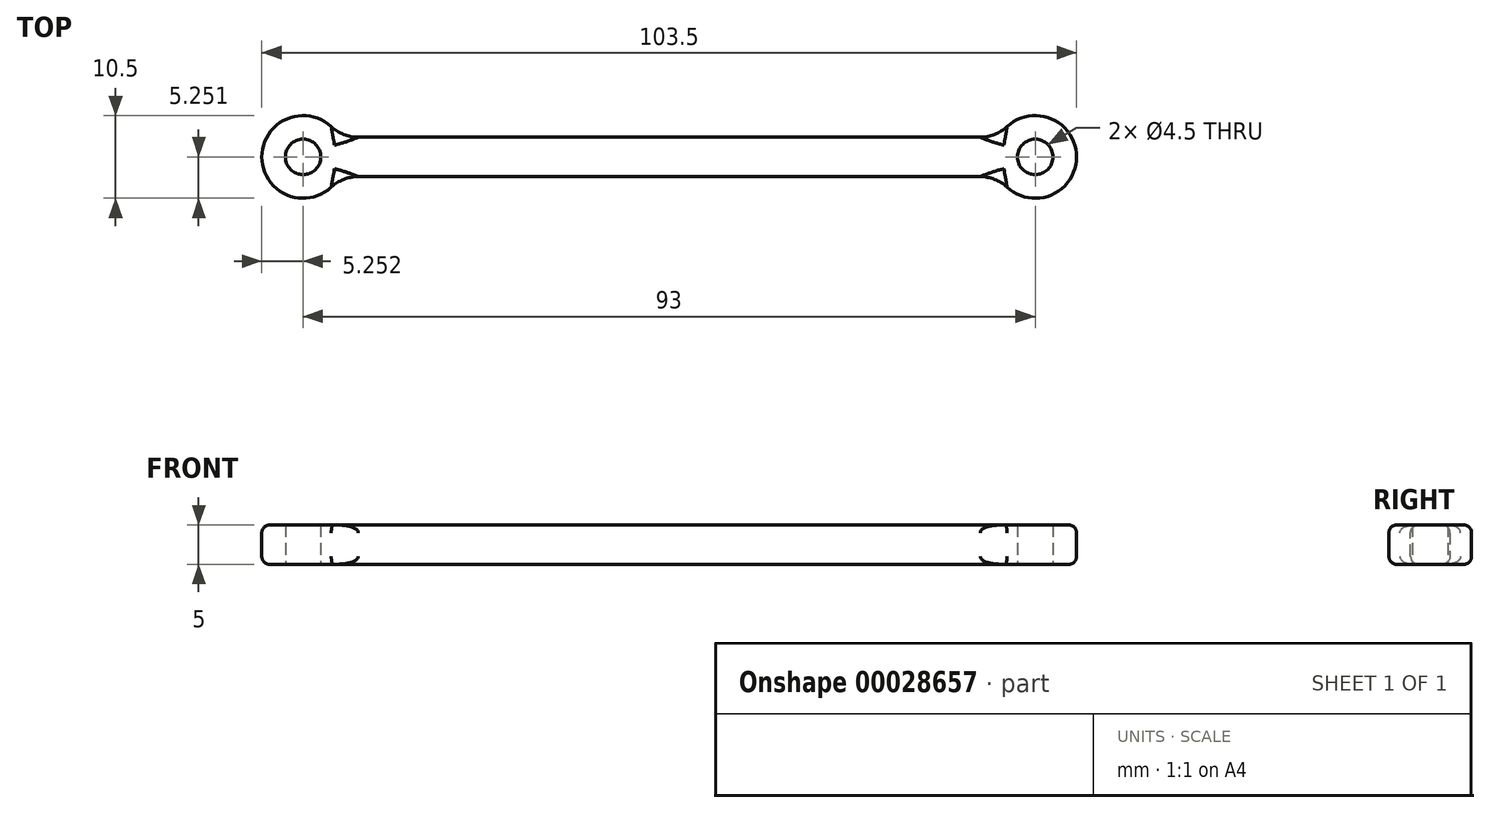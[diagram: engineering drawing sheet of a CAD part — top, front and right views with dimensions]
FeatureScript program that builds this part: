
annotation { "Feature Type Name" : "Feature", "Feature Type Description" : "" }
export const myFeature = defineFeature(function(context is Context, id is Id, definition is map)
    precondition{}
    {
        {
            var Q0;
            Q0=qCreatedBy(makeId("Top.planeOp"),FACE);
            var sketch = newSketch(context, id + "F0", { "sketchPlane" : qUnion([Q0])});
            skLineSegment(sketch, "E0.bottom", {"start": v(-37.64, 2.63) * mm, "end": v(55.36, 2.63) * mm});
            skLineSegment(sketch, "E0.top", {"start": v(-37.64, -2.37) * mm, "end": v(55.36, -2.37) * mm});
            skLineSegment(sketch, "E0.right", {"start": v(55.36, 2.63) * mm, "end": v(55.36, 2.38) * mm});
            skCircle(sketch, "E1", {"center": v(-37.64, 0.13) * mm, "radius": 5.25 * mm});
            skCircle(sketch, "E2", {"center": v(-37.64, 0.13) * mm, "radius": 2.25 * mm});
            skCircle(sketch, "E3", {"center": v(55.36, 0.13) * mm, "radius": 5.25 * mm});
            skCircle(sketch, "E4", {"center": v(55.36, 0.13) * mm, "radius": 2.25 * mm});
            skLineSegment(sketch, "E5.trimOffspring", {"start": v(-37.64, -2.12) * mm, "end": v(-37.64, -2.37) * mm});
            skLineSegment(sketch, "E6.trimOffspring", {"start": v(55.36, -2.12) * mm, "end": v(55.36, -2.37) * mm});
            skSolve(sketch);
        }
        {
            var Q0;
            Q0 = qSketchRegion(id + "F0", true);
            extrude(context, id + "F1", {"entities" : qUnion([Q0]), "depth" : 5 * mm});
        }
        {
            var Q0;
            Q0=makeQuery(id+"F1.opExtrude","CAP_EDGE",EDGE,{"disambiguationData":[OSD([sQuery(id+"F0.wireOp",EDGE,"E0.bottom")])],"isStart":false});
            var Q1;
            Q1=makeQuery(id+"F1.opExtrude","CAP_EDGE",EDGE,{"disambiguationData":[OSD([sQuery(id+"F0.wireOp",EDGE,"E3")])],"isStart":false});
            var Q2;
            Q2=makeQuery(id+"F1.opExtrude","CAP_EDGE",EDGE,{"disambiguationData":[OSD([sQuery(id+"F0.wireOp",EDGE,"E0.top")])],"isStart":false});
            var Q3;
            Q3=makeQuery(id+"F1.opExtrude","CAP_EDGE",EDGE,{"disambiguationData":[OSD([sQuery(id+"F0.wireOp",EDGE,"E1")])],"isStart":false});
            var Q4;
            Q4=makeQuery(id+"F1.opExtrude","CAP_EDGE",EDGE,{"disambiguationData":[OSD([sQuery(id+"F0.wireOp",EDGE,"E1")])],"isStart":true});
            var Q5;
            Q5=makeQuery(id+"F1.opExtrude","CAP_EDGE",EDGE,{"disambiguationData":[OSD([sQuery(id+"F0.wireOp",EDGE,"E0.top")])],"isStart":true});
            var Q6;
            Q6=makeQuery(id+"F1.opExtrude","CAP_EDGE",EDGE,{"disambiguationData":[OSD([sQuery(id+"F0.wireOp",EDGE,"E0.bottom")])],"isStart":true});
            var Q7;
            Q7=makeQuery(id+"F1.opExtrude","CAP_EDGE",EDGE,{"disambiguationData":[OSD([sQuery(id+"F0.wireOp",EDGE,"E3")])],"isStart":true});
            fillet(context, id + "F2", {"entities" : qUnion([Q0, Q1, Q2, Q3, Q4, Q5, Q6, Q7]), "radius" : 1 * mm, "tangentPropagation" : true, "allowEdgeOverflow" : false});
        }
        {
            var Q0;
            Q0=makeQuery(id+"F1.opExtrude","SWEPT_EDGE",EDGE,{"disambiguationData":[OSD([sQuery(id+"F0.wireOp",EDGE,"E0.bottom"),sQuery(id+"F0.wireOp",EDGE,"E1")])]});
            var Q1;
            Q1=makeQuery(id+"F1.opExtrude","SWEPT_EDGE",EDGE,{"disambiguationData":[OSD([sQuery(id+"F0.wireOp",EDGE,"E0.bottom"),sQuery(id+"F0.wireOp",EDGE,"E3")])]});
            var Q2;
            Q2=makeQuery(id+"F1.opExtrude","SWEPT_EDGE",EDGE,{"disambiguationData":[OSD([sQuery(id+"F0.wireOp",EDGE,"E0.top"),sQuery(id+"F0.wireOp",EDGE,"E1")])]});
            var Q3;
            Q3=makeQuery(id+"F1.opExtrude","SWEPT_EDGE",EDGE,{"disambiguationData":[OSD([sQuery(id+"F0.wireOp",EDGE,"E0.top"),sQuery(id+"F0.wireOp",EDGE,"E3")])]});
            fillet(context, id + "F3", {"entities" : qUnion([Q0, Q1, Q2, Q3]), "radius" : 5 * mm, "tangentPropagation" : true, "allowEdgeOverflow" : false});
        }
    });
